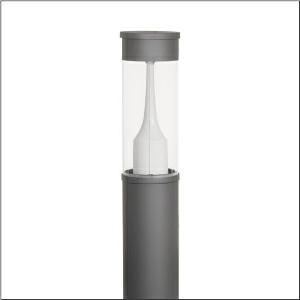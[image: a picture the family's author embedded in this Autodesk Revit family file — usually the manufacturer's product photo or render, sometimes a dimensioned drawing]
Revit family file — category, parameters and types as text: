
# Revit family: city-light_400_iq___p1_0a_5xa5305ff14h_0bc5
name_source: partatom
category: Lighting Fixtures
units: mm (PartAtom-declared; Revit-internal decimal feet)

## family parameters
Cut with Voids When Loaded = No
Host = Face
Light Source = No
Part Type = Normal
Room Calculation Point = No
Round Connector Dimension = Use Diameter
Shared = No

## types (1)
- --- (1 x LED, 1510 lm, 10.5 W, 3000K)
    Apparent Load = 11 VA
    CIE Flux Codes = 32 61 90 93 100
    Color Rendering = 70
    Color Temperature = 3000K
    Default Elevation = 1800 mm
    Description = City-Light 400 iQ, light pillar, Module 540 iQ-SR, primary light control with 3 zone facetted reflector, of plastic, silver coated, highly specular, structured, primary optical cover: cover, of PMMA, transparent, light distribution: P1.0a, primary light characteristic: strongly asymmetric, LED, High Power LED, rated luminous flux: 1.510lm, luminous efficacy: 144lm/W, light colour: 730, colour temperature: 3000K, control gear: ECG iQ, control: Auto-Match, Temp-Guard, Lumen-Switch, Night-Set, Smart-Wire, Light-Fading, Desk-Remote (wireless, voltage-free reading and setting of iQ features in the workshop via application-optimized NFC function/RFID function), optimised constant luminous flux control (CLO 2.0), Street-Remote, presetting dimming logarithmic, with terminal, 6-pole, max. 2.5mm², mains connection: 230..240V, AC, 50/60Hz, start of lifetime: 11W, end of service life: 11W, reduction: 5W, luminaire housing, cylindrical, of extruded aluminium section, coated, Siteco® metallic grey (DB 702S), length: 4.694mm, diameter: 200mm, Module 540 iQ-SR, traffic white (RAL 9016), equipment: standard, protection rating (complete): IP65, insulation class (complete): insulation class II (safety insulation), certification: CE, ENEC, VDE, packaging unit: 1 piece

Light Distribution: P1.0a
    Height = 500 mm
    Lamp = 1 x LED
    Lamp Light Flux = 1510 lm
    Lamp Power = 10.5 W
    Lamp count = 1
    Length = 200 mm  [stored 0.656168 ft]
    Luminous efficacy = 144 lm/W
    Manufacturer = Siteco
    ModVariant = No
    Model = 5XA5305FF14H
    Mounting Place = Floor
    Mounting Type = Freestanding
    Number of Poles = 1
    OnlyDefault = Yes
    Power Factor = 1
    Product Name = City-Light 400 iQ | P1.0a
    Product group = light pillar
    ProductGroupID = 1303
    Protection Class = Protection class II
    Protection Degree = IP 65
    RLX_Detail_Level = 1
    RLX_Emergency_Light_Flux = 0 lm
    RLX_Emergency_Type = 0
    RLX_Emergency_Type_DB = No
    RlxData = <blob elided: 75441 chars, md5=4d61aabe>
    Socket = socket
    Standby Power = 0 W
    System Light Flux = 1510 lm
    System Power = 11 W
    Type Comments = factory setting: luminous flux: 100 % | dim-lin: 254 | 419 mA
    Type Image = l_1006914.jpg
    URL = http://relux.com
    VarID = @adj_109575
    Voltage = 0 V
    Weight = 0.00 kg
    Width = 0 mm  [stored 0 ft]

note: [stored X ft] marks values corroborated as IEEE doubles in the binary element streams (Revit-internal decimal feet)

## geometry (parser evidence)
native form markers: Blend x4, Sweep x8
no freeform markers — native parametric forms only
